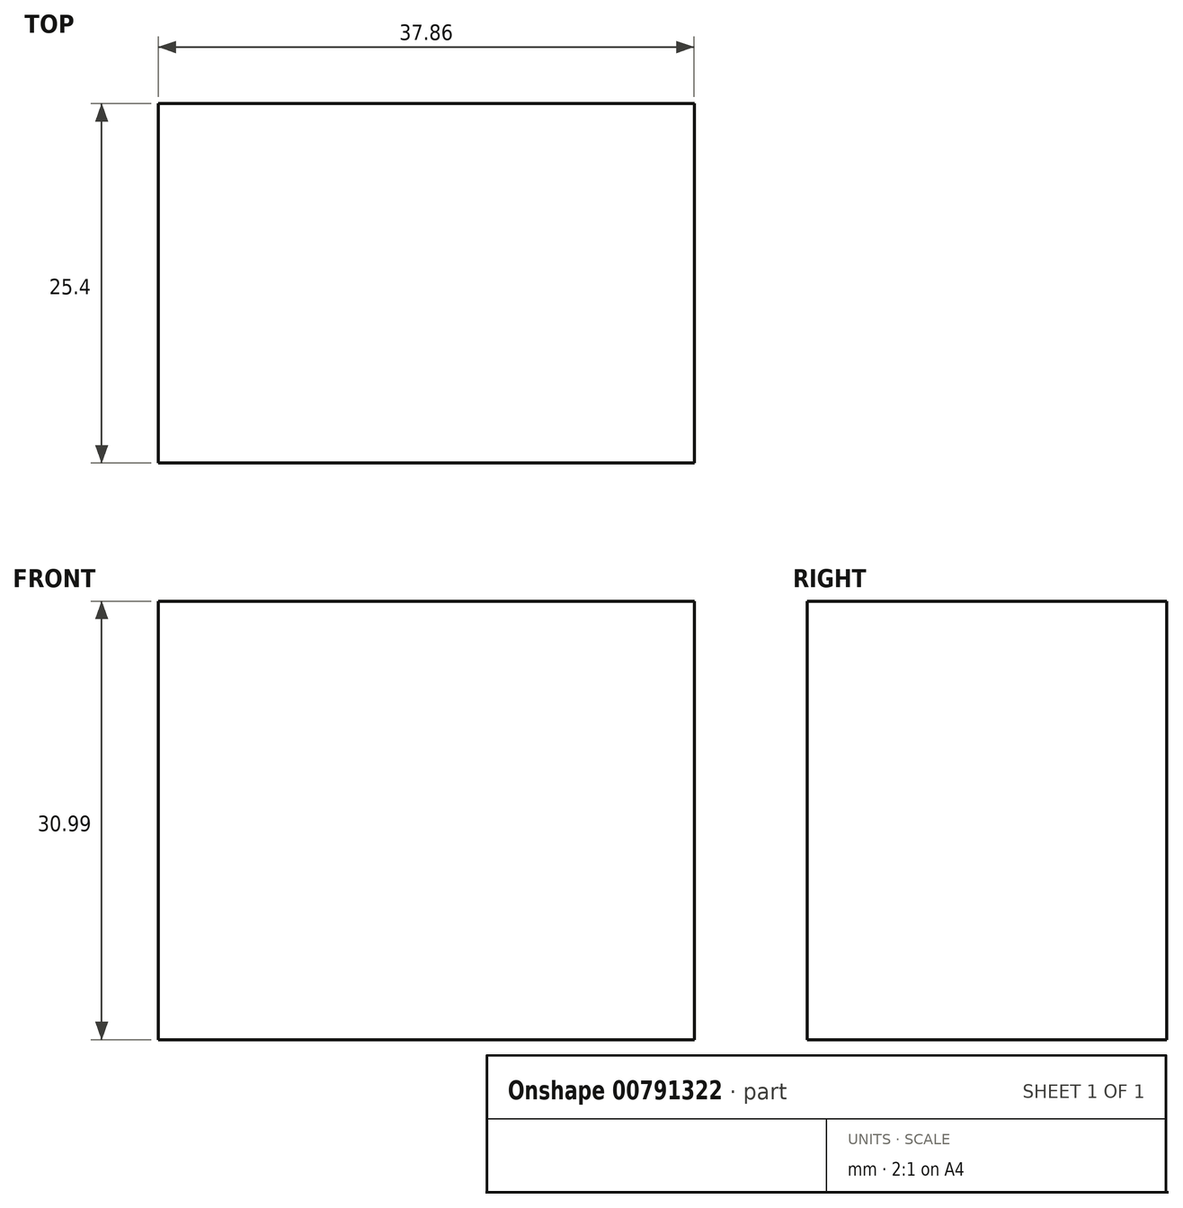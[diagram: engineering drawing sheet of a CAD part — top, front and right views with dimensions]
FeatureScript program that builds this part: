
annotation { "Feature Type Name" : "Feature", "Feature Type Description" : "" }
export const myFeature = defineFeature(function(context is Context, id is Id, definition is map)
    precondition{}
    {
        {
            var Q0;
            Q0=qCreatedBy(makeId("Front.planeOp"),FACE);
            var sketch = newSketch(context, id + "F0", { "sketchPlane" : qUnion([Q0])});
            skLineSegment(sketch, "E0.bottom", {"start": v(-92.63, 38.62) * mm, "end": v(-54.77, 38.62) * mm});
            skLineSegment(sketch, "E0.top", {"start": v(-92.63, 7.63) * mm, "end": v(-54.77, 7.63) * mm});
            skLineSegment(sketch, "E0.left", {"start": v(-92.63, 38.62) * mm, "end": v(-92.63, 7.63) * mm});
            skLineSegment(sketch, "E0.right", {"start": v(-54.77, 38.62) * mm, "end": v(-54.77, 7.63) * mm});
            skSolve(sketch);
        }
        {
            var Q0;
            Q0 = qSketchRegion(id + "F0", true);
            extrude(context, id + "F1", {"entities" : qUnion([Q0]), "depth" : 25.4 * mm, "offsetDistance" : 25.4 * mm});
        }
    });
